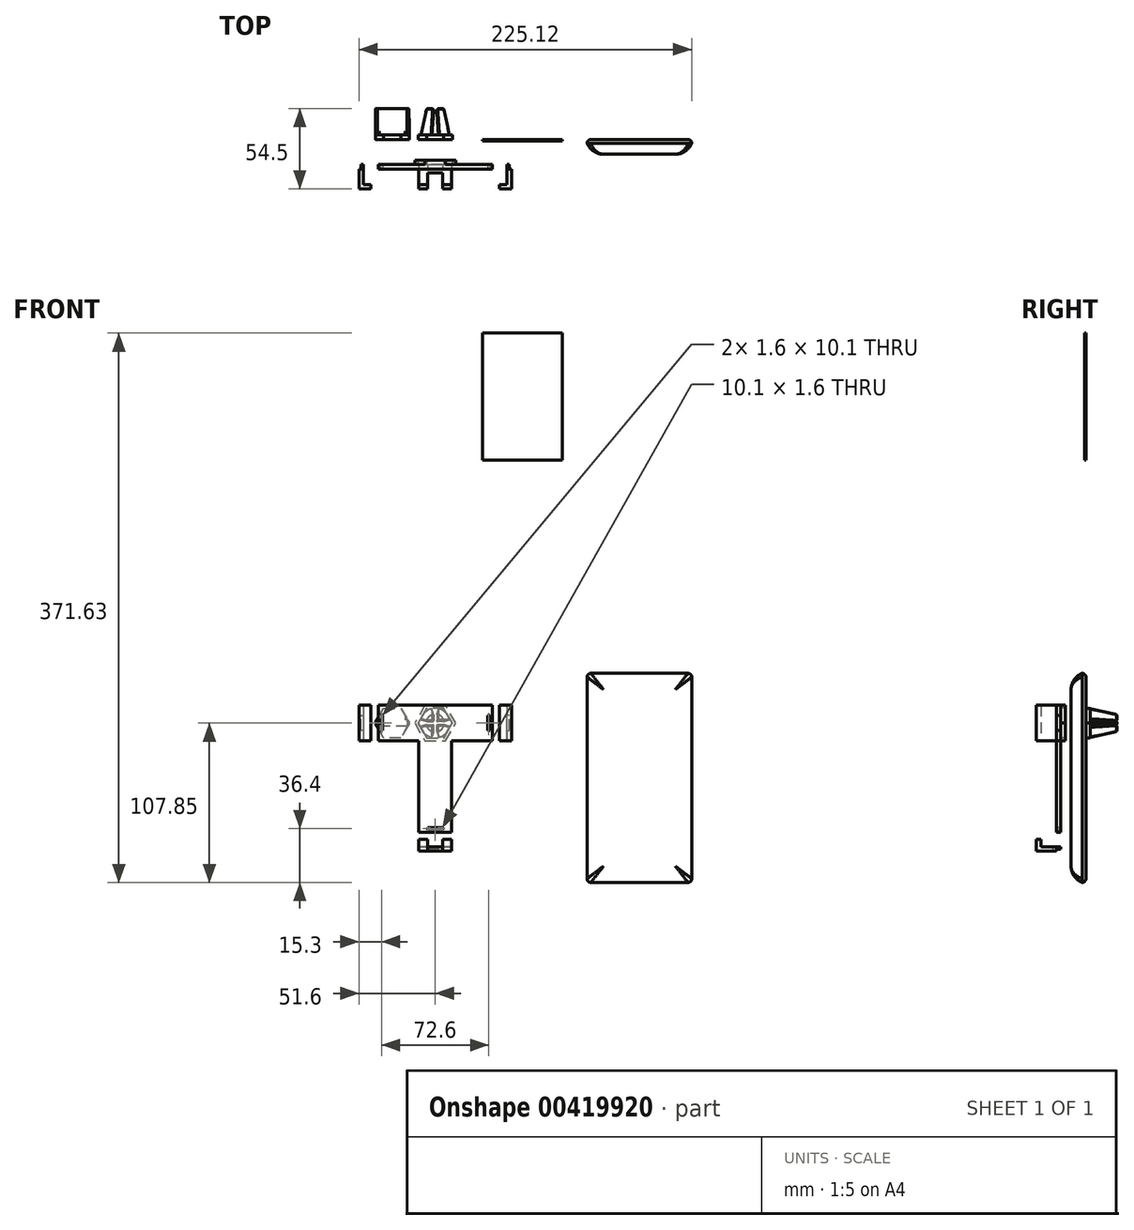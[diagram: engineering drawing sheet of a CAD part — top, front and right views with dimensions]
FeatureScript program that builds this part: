
annotation { "Feature Type Name" : "Feature", "Feature Type Description" : "" }
export const myFeature = defineFeature(function(context is Context, id is Id, definition is map)
    precondition{}
    {
        {
            assignVariable(context, id + "F0", {"name" : "depth_phone", "anyValue" : 10});
        }
        {
            var Q0;
            Q0=qCreatedBy(makeId("Front.planeOp"),FACE);
            var sketch = newSketch(context, id + "F1", { "sketchPlane" : qUnion([Q0])});
            skCircle(sketch, "E0", {"center": v(0, 0) * mm, "radius": 10 * mm});
            skSolve(sketch);
        }
        {
            var Q0;
            Q0=qSketchRegion(id+"F1",true);
            extrude(context, id + "F2", {"entities" : qUnion([Q0]), "oppositeDirection" : true, "depth" : 3 * mm});
        }
        {
            var Q0;
            Q0=makeQuery(id+"F2.opExtrude","CAP_FACE",FACE,{"disambiguationData":[OSD([sQuery(id+"F1.wireOp",EDGE,"E0")])],"isStart":false});
            var sketch = newSketch(context, id + "F3", { "sketchPlane" : qUnion([Q0])});
            skLineSegment(sketch, "E1.top", {"start": v(-9.75, 2.2) * mm, "end": v(-2.2, 2.2) * mm});
            skLineSegment(sketch, "E1.right", {"start": v(-2.2, 9.75) * mm, "end": v(-2.2, 2.2) * mm});
            skArc(sketch, "E2", {"start": v(-2.2, 9.75) * mm, "mid": v(-7.07, 7.07) * mm, "end": v(-9.75, 2.2) * mm});
            skLineSegment(sketch, "E3.1.0", {"start": v(-9.75, -2.2) * mm, "end": v(-2.2, -2.2) * mm});
            skLineSegment(sketch, "E3.1.1", {"start": v(-2.2, -9.75) * mm, "end": v(-2.2, -2.2) * mm});
            skArc(sketch, "E3.1.2", {"start": v(-9.75, -2.2) * mm, "mid": v(-7.07, -7.07) * mm, "end": v(-2.2, -9.75) * mm});
            skLineSegment(sketch, "E3.2.0", {"start": v(2.2, -9.75) * mm, "end": v(2.2, -2.2) * mm});
            skLineSegment(sketch, "E3.2.1", {"start": v(9.75, -2.2) * mm, "end": v(2.2, -2.2) * mm});
            skArc(sketch, "E3.2.2", {"start": v(2.2, -9.75) * mm, "mid": v(7.07, -7.07) * mm, "end": v(9.75, -2.2) * mm});
            skLineSegment(sketch, "E4.2.3.0", {"start": v(9.75, 2.2) * mm, "end": v(2.2, 2.2) * mm});
            skLineSegment(sketch, "E4.3.3.0", {"start": v(2.2, 9.75) * mm, "end": v(2.2, 2.2) * mm});
            skArc(sketch, "E4.6.3.0", {"start": v(9.75, 2.2) * mm, "mid": v(7.07, 7.07) * mm, "end": v(2.2, 9.75) * mm});
            skSolve(sketch);
        }
        {
            var Q0;
            Q0=makeQuery(id+"F3.imprint","IMPRINT",FACE,{"disambiguationData":[TD([[makeQuery(id+"F3.imprint","IMPRINT",EDGE,{"derivedFrom":sQuery(id+"F3.wireOp",EDGE,"E1.top")}),-1.0]])]});
            cPlane(context, id + "F4", {"entities" : qUnion([Q0]), "cplaneType" : CPlaneType.OFFSET, "offset" : 18 * mm, "width" : 150 * mm, "height" : 150 * mm});
        }
        {
            var Q0;
            Q0=qCreatedBy(id+"F4.planeOp",FACE);
            var sketch = newSketch(context, id + "F5", { "sketchPlane" : qUnion([Q0])});
            skLineSegment(sketch, "E5.top", {"start": v(-5.92, 1) * mm, "end": v(-1, 1) * mm});
            skLineSegment(sketch, "E5.right", {"start": v(-1, 5.92) * mm, "end": v(-1, 1) * mm});
            skArc(sketch, "E6", {"start": v(-1, 5.92) * mm, "mid": v(-4.24, 4.24) * mm, "end": v(-5.92, 1) * mm});
            skLineSegment(sketch, "E7.1.0", {"start": v(-5.92, -1) * mm, "end": v(-1, -1) * mm});
            skLineSegment(sketch, "E7.1.1", {"start": v(-1, -5.92) * mm, "end": v(-1, -1) * mm});
            skArc(sketch, "E7.1.2", {"start": v(-5.92, -1) * mm, "mid": v(-4.24, -4.24) * mm, "end": v(-1, -5.92) * mm});
            skLineSegment(sketch, "E7.2.0", {"start": v(1, -5.92) * mm, "end": v(1, -1) * mm});
            skLineSegment(sketch, "E7.2.1", {"start": v(5.92, -1) * mm, "end": v(1, -1) * mm});
            skArc(sketch, "E7.2.2", {"start": v(1, -5.92) * mm, "mid": v(4.24, -4.24) * mm, "end": v(5.92, -1) * mm});
            skLineSegment(sketch, "E7.3.0", {"start": v(5.92, 1) * mm, "end": v(1, 1) * mm});
            skLineSegment(sketch, "E7.3.1", {"start": v(1, 5.92) * mm, "end": v(1, 1) * mm});
            skArc(sketch, "E7.3.2", {"start": v(5.92, 1) * mm, "mid": v(4.24, 4.24) * mm, "end": v(1, 5.92) * mm});
            skSolve(sketch);
        }
        {
            var Q1;
            Q1=makeQuery(id+"F5.imprint","IMPRINT",FACE,{"disambiguationData":[TD([[makeQuery(id+"F5.imprint","IMPRINT",EDGE,{"derivedFrom":sQuery(id+"F5.wireOp",EDGE,"E5.top")}),1.0]])]});
            var Q2;
            Q2=makeQuery(id+"F3.imprint","IMPRINT",FACE,{"disambiguationData":[TD([[makeQuery(id+"F3.imprint","IMPRINT",EDGE,{"derivedFrom":sQuery(id+"F3.wireOp",EDGE,"E1.top")}),1.0]])]});
            loft(context, id + "F6", {"operationType" : NewBodyOperationType.ADD, "sheetProfilesArray" : [{ "sheetProfileEntities" : qUnion([Q1]) }, { "sheetProfileEntities" : qUnion([Q2]) }]});
        }
        {
            var Q1;
            Q1=makeQuery(id+"F3.imprint","IMPRINT",FACE,{"disambiguationData":[TD([[makeQuery(id+"F3.imprint","IMPRINT",EDGE,{"derivedFrom":sQuery(id+"F3.wireOp",EDGE,"E4.2.3.0")}),-1.0]])]});
            var Q2;
            Q2=makeQuery(id+"F5.imprint","IMPRINT",FACE,{"disambiguationData":[TD([[makeQuery(id+"F5.imprint","IMPRINT",EDGE,{"derivedFrom":sQuery(id+"F5.wireOp",EDGE,"E7.3.0")}),-1.0]])]});
            loft(context, id + "F7", {"operationType" : NewBodyOperationType.ADD, "sheetProfilesArray" : [{ "sheetProfileEntities" : qUnion([Q1]) }, { "sheetProfileEntities" : qUnion([Q2]) }]});
        }
        {
            var Q1;
            Q1=makeQuery(id+"F3.imprint","IMPRINT",FACE,{"disambiguationData":[TD([[makeQuery(id+"F3.imprint","IMPRINT",EDGE,{"derivedFrom":sQuery(id+"F3.wireOp",EDGE,"E3.1.0")}),-1.0]])]});
            var Q2;
            Q2=makeQuery(id+"F5.imprint","IMPRINT",FACE,{"disambiguationData":[TD([[makeQuery(id+"F5.imprint","IMPRINT",EDGE,{"derivedFrom":sQuery(id+"F5.wireOp",EDGE,"E7.1.0")}),-1.0]])]});
            loft(context, id + "F8", {"operationType" : NewBodyOperationType.ADD, "sheetProfilesArray" : [{ "sheetProfileEntities" : qUnion([Q1]) }, { "sheetProfileEntities" : qUnion([Q2]) }]});
        }
        {
            var Q1;
            Q1=makeQuery(id+"F3.imprint","IMPRINT",FACE,{"disambiguationData":[TD([[makeQuery(id+"F3.imprint","IMPRINT",EDGE,{"derivedFrom":sQuery(id+"F3.wireOp",EDGE,"E3.2.0")}),-1.0]])]});
            var Q2;
            Q2=makeQuery(id+"F5.imprint","IMPRINT",FACE,{"disambiguationData":[TD([[makeQuery(id+"F5.imprint","IMPRINT",EDGE,{"derivedFrom":sQuery(id+"F5.wireOp",EDGE,"E7.2.0")}),-1.0]])]});
            loft(context, id + "F9", {"operationType" : NewBodyOperationType.ADD, "sheetProfilesArray" : [{ "sheetProfileEntities" : qUnion([Q1]) }, { "sheetProfileEntities" : qUnion([Q2]) }]});
        }
        {
            var Q0;
            {var subQ0=sQuery(id+"F5.wireOp",EDGE,"E6");var subQ1=sQuery(id+"F5.wireOp",EDGE,"E5.right");var subQ2=sQuery(id+"F5.wireOp",EDGE,"E5.top");Q0=makeQuery(id+"F6.opLoft","MID_CAP_EDGE",EDGE,{"disambiguationData":[OSD([subQ2,subQ1,subQ0]),TDD([makeQuery(id+"F5.imprint","INTERSECT",VERTEX,{"derivedFrom":[subQ2,subQ0]}),makeQuery(id+"F5.imprint","INTERSECT",VERTEX,{"derivedFrom":[subQ1,subQ0]}),makeQuery(id+"F5.imprint","IMPRINT",EDGE,{"derivedFrom":subQ0})])],"capPos":0.0});}
            var Q1;
            Q1=makeQuery(id+"F6.opLoft","SWEPT_EDGE",EDGE,{"disambiguationData":[OSD([sQuery(id+"F3.wireOp",EDGE,"E1.right"),sQuery(id+"F3.wireOp",EDGE,"E2"),sQuery(id+"F5.wireOp",EDGE,"E5.right"),sQuery(id+"F5.wireOp",EDGE,"E6")])]});
            var Q2;
            Q2=makeQuery(id+"F6.opLoft","SWEPT_EDGE",EDGE,{"disambiguationData":[OSD([sQuery(id+"F3.wireOp",EDGE,"E1.top"),sQuery(id+"F3.wireOp",EDGE,"E1.right"),sQuery(id+"F5.wireOp",EDGE,"E5.top"),sQuery(id+"F5.wireOp",EDGE,"E5.right")])]});
            var Q3;
            Q3=makeQuery(id+"F6.opLoft","SWEPT_EDGE",EDGE,{"disambiguationData":[OSD([sQuery(id+"F3.wireOp",EDGE,"E1.top"),sQuery(id+"F3.wireOp",EDGE,"E2"),sQuery(id+"F5.wireOp",EDGE,"E5.top"),sQuery(id+"F5.wireOp",EDGE,"E6")])]});
            var Q4;
            {var subQ0=sQuery(id+"F5.wireOp",EDGE,"E7.1.2");var subQ1=sQuery(id+"F5.wireOp",EDGE,"E7.1.1");var subQ2=sQuery(id+"F5.wireOp",EDGE,"E7.1.0");Q4=makeQuery(id+"F8.opLoft","MID_CAP_EDGE",EDGE,{"disambiguationData":[OSD([subQ2,subQ1,subQ0]),TDD([makeQuery(id+"F5.imprint","INTERSECT",VERTEX,{"derivedFrom":[subQ2,subQ0]}),makeQuery(id+"F5.imprint","INTERSECT",VERTEX,{"derivedFrom":[subQ1,subQ0]}),makeQuery(id+"F5.imprint","IMPRINT",EDGE,{"derivedFrom":subQ0})])],"capPos":1.0});}
            var Q5;
            Q5=makeQuery(id+"F8.opLoft","SWEPT_EDGE",EDGE,{"disambiguationData":[OSD([sQuery(id+"F3.wireOp",EDGE,"E3.1.0"),sQuery(id+"F3.wireOp",EDGE,"E3.1.2"),sQuery(id+"F5.wireOp",EDGE,"E7.1.0"),sQuery(id+"F5.wireOp",EDGE,"E7.1.2")])]});
            var Q6;
            Q6=makeQuery(id+"F8.opLoft","SWEPT_EDGE",EDGE,{"disambiguationData":[OSD([sQuery(id+"F3.wireOp",EDGE,"E3.1.0"),sQuery(id+"F3.wireOp",EDGE,"E3.1.1"),sQuery(id+"F5.wireOp",EDGE,"E7.1.0"),sQuery(id+"F5.wireOp",EDGE,"E7.1.1")])]});
            var Q7;
            Q7=makeQuery(id+"F8.opLoft","SWEPT_EDGE",EDGE,{"disambiguationData":[OSD([sQuery(id+"F3.wireOp",EDGE,"E3.1.1"),sQuery(id+"F3.wireOp",EDGE,"E3.1.2"),sQuery(id+"F5.wireOp",EDGE,"E7.1.1"),sQuery(id+"F5.wireOp",EDGE,"E7.1.2")])]});
            var Q8;
            {var subQ0=sQuery(id+"F5.wireOp",EDGE,"E7.2.2");var subQ1=sQuery(id+"F5.wireOp",EDGE,"E7.2.1");var subQ2=sQuery(id+"F5.wireOp",EDGE,"E7.2.0");Q8=makeQuery(id+"F9.opLoft","MID_CAP_EDGE",EDGE,{"disambiguationData":[OSD([subQ2,subQ1,subQ0]),TDD([makeQuery(id+"F5.imprint","INTERSECT",VERTEX,{"derivedFrom":[subQ2,subQ0]}),makeQuery(id+"F5.imprint","INTERSECT",VERTEX,{"derivedFrom":[subQ1,subQ0]}),makeQuery(id+"F5.imprint","IMPRINT",EDGE,{"derivedFrom":subQ0})])],"capPos":1.0});}
            var Q9;
            Q9=makeQuery(id+"F9.opLoft","SWEPT_EDGE",EDGE,{"disambiguationData":[OSD([sQuery(id+"F3.wireOp",EDGE,"E3.2.0"),sQuery(id+"F3.wireOp",EDGE,"E3.2.2"),sQuery(id+"F5.wireOp",EDGE,"E7.2.0"),sQuery(id+"F5.wireOp",EDGE,"E7.2.2")])]});
            var Q10;
            Q10=makeQuery(id+"F9.opLoft","SWEPT_EDGE",EDGE,{"disambiguationData":[OSD([sQuery(id+"F3.wireOp",EDGE,"E3.2.1"),sQuery(id+"F3.wireOp",EDGE,"E3.2.2"),sQuery(id+"F5.wireOp",EDGE,"E7.2.1"),sQuery(id+"F5.wireOp",EDGE,"E7.2.2")])]});
            var Q11;
            Q11=makeQuery(id+"F9.opLoft","SWEPT_EDGE",EDGE,{"disambiguationData":[OSD([sQuery(id+"F3.wireOp",EDGE,"E3.2.0"),sQuery(id+"F3.wireOp",EDGE,"E3.2.1"),sQuery(id+"F5.wireOp",EDGE,"E7.2.0"),sQuery(id+"F5.wireOp",EDGE,"E7.2.1")])]});
            var Q12;
            {var subQ0=sQuery(id+"F5.wireOp",EDGE,"E7.3.2");var subQ1=sQuery(id+"F5.wireOp",EDGE,"E7.3.1");var subQ2=sQuery(id+"F5.wireOp",EDGE,"E7.3.0");Q12=makeQuery(id+"F7.opLoft","MID_CAP_EDGE",EDGE,{"disambiguationData":[OSD([subQ2,subQ1,subQ0]),TDD([makeQuery(id+"F5.imprint","INTERSECT",VERTEX,{"derivedFrom":[subQ2,subQ0]}),makeQuery(id+"F5.imprint","INTERSECT",VERTEX,{"derivedFrom":[subQ1,subQ0]}),makeQuery(id+"F5.imprint","IMPRINT",EDGE,{"derivedFrom":subQ0})])],"capPos":1.0});}
            var Q13;
            Q13=makeQuery(id+"F7.opLoft","SWEPT_EDGE",EDGE,{"disambiguationData":[OSD([sQuery(id+"F3.wireOp",EDGE,"E4.2.3.0"),sQuery(id+"F3.wireOp",EDGE,"E4.3.3.0"),sQuery(id+"F5.wireOp",EDGE,"E7.3.0"),sQuery(id+"F5.wireOp",EDGE,"E7.3.1")])]});
            var Q14;
            Q14=makeQuery(id+"F7.opLoft","SWEPT_EDGE",EDGE,{"disambiguationData":[OSD([sQuery(id+"F3.wireOp",EDGE,"E4.2.3.0"),sQuery(id+"F3.wireOp",EDGE,"E4.6.3.0"),sQuery(id+"F5.wireOp",EDGE,"E7.3.0"),sQuery(id+"F5.wireOp",EDGE,"E7.3.2")])]});
            var Q15;
            Q15=makeQuery(id+"F7.opLoft","SWEPT_EDGE",EDGE,{"disambiguationData":[OSD([sQuery(id+"F3.wireOp",EDGE,"E4.3.3.0"),sQuery(id+"F3.wireOp",EDGE,"E4.6.3.0"),sQuery(id+"F5.wireOp",EDGE,"E7.3.1"),sQuery(id+"F5.wireOp",EDGE,"E7.3.2")])]});
            fillet(context, id + "F10", {"entities" : qUnion([Q0, Q1, Q2, Q3, Q4, Q5, Q6, Q7, Q8, Q9, Q10, Q11, Q12, Q13, Q14, Q15]), "radius" : .5 * mm, "tangentPropagation" : true, "allowEdgeOverflow" : false});
        }
        {
            var Q0;
            Q0=qCreatedBy(makeId("Front.planeOp"),FACE);
            var sketch = newSketch(context, id + "F11", { "sketchPlane" : qUnion([Q0])});
            skLineSegment(sketch, "E8.bottom", {"start": v(86.03, 177.78) * mm, "end": v(32.03, 177.78) * mm});
            skLineSegment(sketch, "E8.top", {"start": v(86.03, 263.78) * mm, "end": v(32.03, 263.78) * mm});
            skLineSegment(sketch, "E8.left", {"start": v(86.03, 177.78) * mm, "end": v(86.03, 263.78) * mm});
            skLineSegment(sketch, "E8.right", {"start": v(32.03, 177.78) * mm, "end": v(32.03, 263.78) * mm});
            skSolve(sketch);
        }
        {
            var Q0;
            Q0=makeQuery(id+"F11.imprint","IMPRINT",FACE,{"disambiguationData":[TD([[makeQuery(id+"F11.imprint","IMPRINT",EDGE,{"derivedFrom":sQuery(id+"F11.wireOp",EDGE,"E8.bottom")}),-1.0]])]});
            extrude(context, id + "F12", {"entities" : qUnion([Q0]), "depth" : 1 * mm});
        }
        {
            var Q0;
            {var subQ0=sQuery(id+"F5.wireOp",EDGE,"E5.right");var subQ1=sQuery(id+"F5.wireOp",EDGE,"E6");var subQ2=sQuery(id+"F5.wireOp",EDGE,"E5.top");Q0=makeQuery(id+"F6.opLoft","MID_CAP_EDGE",EDGE,{"disambiguationData":[OSD([subQ2,subQ0,subQ1]),TDD([makeQuery(id+"F5.imprint","INTERSECT",VERTEX,{"derivedFrom":[subQ2,subQ0]}),makeQuery(id+"F5.imprint","INTERSECT",VERTEX,{"derivedFrom":[subQ0,subQ1]}),makeQuery(id+"F5.imprint","IMPRINT",EDGE,{"derivedFrom":subQ0})])],"capPos":0.0});}
            var Q1;
            {var subQ0=sQuery(id+"F5.wireOp",EDGE,"E5.top");var subQ1=sQuery(id+"F5.wireOp",EDGE,"E5.right");var subQ2=sQuery(id+"F5.wireOp",EDGE,"E6");Q1=makeQuery(id+"F6.opLoft","MID_CAP_EDGE",EDGE,{"disambiguationData":[OSD([subQ0,subQ1,subQ2]),TDD([makeQuery(id+"F5.imprint","INTERSECT",VERTEX,{"derivedFrom":[subQ0,subQ2]}),makeQuery(id+"F5.imprint","INTERSECT",VERTEX,{"derivedFrom":[subQ0,subQ1]}),makeQuery(id+"F5.imprint","IMPRINT",EDGE,{"derivedFrom":subQ0})])],"capPos":0.0});}
            var Q2;
            {var subQ0=sQuery(id+"F5.wireOp",EDGE,"E7.1.0");var subQ1=sQuery(id+"F5.wireOp",EDGE,"E7.1.1");var subQ2=sQuery(id+"F5.wireOp",EDGE,"E7.1.2");Q2=makeQuery(id+"F8.opLoft","MID_CAP_EDGE",EDGE,{"disambiguationData":[OSD([subQ0,subQ1,subQ2]),TDD([makeQuery(id+"F5.imprint","INTERSECT",VERTEX,{"derivedFrom":[subQ0,subQ2]}),makeQuery(id+"F5.imprint","INTERSECT",VERTEX,{"derivedFrom":[subQ0,subQ1]}),makeQuery(id+"F5.imprint","IMPRINT",EDGE,{"derivedFrom":subQ0})])],"capPos":1.0});}
            var Q3;
            {var subQ0=sQuery(id+"F5.wireOp",EDGE,"E7.1.1");var subQ1=sQuery(id+"F5.wireOp",EDGE,"E7.1.2");var subQ2=sQuery(id+"F5.wireOp",EDGE,"E7.1.0");Q3=makeQuery(id+"F8.opLoft","MID_CAP_EDGE",EDGE,{"disambiguationData":[OSD([subQ2,subQ0,subQ1]),TDD([makeQuery(id+"F5.imprint","INTERSECT",VERTEX,{"derivedFrom":[subQ2,subQ0]}),makeQuery(id+"F5.imprint","INTERSECT",VERTEX,{"derivedFrom":[subQ0,subQ1]}),makeQuery(id+"F5.imprint","IMPRINT",EDGE,{"derivedFrom":subQ0})])],"capPos":1.0});}
            var Q4;
            {var subQ0=sQuery(id+"F5.wireOp",EDGE,"E7.2.0");var subQ1=sQuery(id+"F5.wireOp",EDGE,"E7.2.1");var subQ2=sQuery(id+"F5.wireOp",EDGE,"E7.2.2");Q4=makeQuery(id+"F9.opLoft","MID_CAP_EDGE",EDGE,{"disambiguationData":[OSD([subQ0,subQ1,subQ2]),TDD([makeQuery(id+"F5.imprint","INTERSECT",VERTEX,{"derivedFrom":[subQ0,subQ2]}),makeQuery(id+"F5.imprint","INTERSECT",VERTEX,{"derivedFrom":[subQ0,subQ1]}),makeQuery(id+"F5.imprint","IMPRINT",EDGE,{"derivedFrom":subQ0})])],"capPos":1.0});}
            var Q5;
            {var subQ0=sQuery(id+"F5.wireOp",EDGE,"E7.2.1");var subQ1=sQuery(id+"F5.wireOp",EDGE,"E7.2.2");var subQ2=sQuery(id+"F5.wireOp",EDGE,"E7.2.0");Q5=makeQuery(id+"F9.opLoft","MID_CAP_EDGE",EDGE,{"disambiguationData":[OSD([subQ2,subQ0,subQ1]),TDD([makeQuery(id+"F5.imprint","INTERSECT",VERTEX,{"derivedFrom":[subQ2,subQ0]}),makeQuery(id+"F5.imprint","INTERSECT",VERTEX,{"derivedFrom":[subQ0,subQ1]}),makeQuery(id+"F5.imprint","IMPRINT",EDGE,{"derivedFrom":subQ0})])],"capPos":1.0});}
            var Q6;
            {var subQ0=sQuery(id+"F5.wireOp",EDGE,"E7.3.0");var subQ1=sQuery(id+"F5.wireOp",EDGE,"E7.3.1");var subQ2=sQuery(id+"F5.wireOp",EDGE,"E7.3.2");Q6=makeQuery(id+"F7.opLoft","MID_CAP_EDGE",EDGE,{"disambiguationData":[OSD([subQ0,subQ1,subQ2]),TDD([makeQuery(id+"F5.imprint","INTERSECT",VERTEX,{"derivedFrom":[subQ0,subQ2]}),makeQuery(id+"F5.imprint","INTERSECT",VERTEX,{"derivedFrom":[subQ0,subQ1]}),makeQuery(id+"F5.imprint","IMPRINT",EDGE,{"derivedFrom":subQ0})])],"capPos":1.0});}
            var Q7;
            {var subQ0=sQuery(id+"F5.wireOp",EDGE,"E7.3.1");var subQ1=sQuery(id+"F5.wireOp",EDGE,"E7.3.2");var subQ2=sQuery(id+"F5.wireOp",EDGE,"E7.3.0");Q7=makeQuery(id+"F7.opLoft","MID_CAP_EDGE",EDGE,{"disambiguationData":[OSD([subQ2,subQ0,subQ1]),TDD([makeQuery(id+"F5.imprint","INTERSECT",VERTEX,{"derivedFrom":[subQ2,subQ0]}),makeQuery(id+"F5.imprint","INTERSECT",VERTEX,{"derivedFrom":[subQ0,subQ1]}),makeQuery(id+"F5.imprint","IMPRINT",EDGE,{"derivedFrom":subQ0})])],"capPos":1.0});}
            fillet(context, id + "F13", {"entities" : qUnion([Q0, Q1, Q2, Q3, Q4, Q5, Q6, Q7]), "radius" : 1.5 * mm, "tangentPropagation" : true, "allowEdgeOverflow" : false});
        }
        {
            var Q0;
            Q0=qCreatedBy(makeId("Front.planeOp"),FACE);
            var sketch = newSketch(context, id + "F14", { "sketchPlane" : qUnion([Q0])});
            skLineSegment(sketch, "E9.bottom", {"start": v(102.82, 33.65) * mm, "end": v(173.52, 33.65) * mm});
            skLineSegment(sketch, "E9.top", {"start": v(102.82, -107.85) * mm, "end": v(173.52, -107.85) * mm});
            skLineSegment(sketch, "E9.left", {"start": v(102.82, 33.65) * mm, "end": v(102.82, -107.85) * mm});
            skLineSegment(sketch, "E9.right", {"start": v(173.52, 33.65) * mm, "end": v(173.52, -107.85) * mm});
            skSolve(sketch);
        }
        {
            var Q0;
            Q0=qSketchRegion(id+"F14",true);
            extrude(context, id + "F15", {"entities" : qUnion([Q0]), "depth" : (getVariable(context, 'depth_phone')) * mm});
        }
        {
            var Q0;
            Q0=makeQuery(id+"F15.opExtrude","SWEPT_EDGE",EDGE,{"disambiguationData":[OSD([sQuery(id+"F14.wireOp",EDGE,"E9.bottom"),sQuery(id+"F14.wireOp",EDGE,"E9.left")])]});
            var Q1;
            Q1=makeQuery(id+"F15.opExtrude","SWEPT_EDGE",EDGE,{"disambiguationData":[OSD([sQuery(id+"F14.wireOp",EDGE,"E9.bottom"),sQuery(id+"F14.wireOp",EDGE,"E9.right")])]});
            var Q2;
            Q2=makeQuery(id+"F15.opExtrude","SWEPT_EDGE",EDGE,{"disambiguationData":[OSD([sQuery(id+"F14.wireOp",EDGE,"E9.top"),sQuery(id+"F14.wireOp",EDGE,"E9.right")])]});
            var Q3;
            Q3=makeQuery(id+"F15.opExtrude","SWEPT_EDGE",EDGE,{"disambiguationData":[OSD([sQuery(id+"F14.wireOp",EDGE,"E9.top"),sQuery(id+"F14.wireOp",EDGE,"E9.left")])]});
            fillet(context, id + "F16", {"entities" : qUnion([Q0, Q1, Q2, Q3]), "radius" : 2.5 * mm, "tangentPropagation" : true, "allowEdgeOverflow" : false});
        }
        {
            var Q0;
            Q0=makeQuery(id+"F15.opExtrude","CAP_EDGE",EDGE,{"disambiguationData":[OSD([sQuery(id+"F14.wireOp",EDGE,"E9.right")])],"isStart":true});
            var Q1;
            Q1=makeQuery(id+"F15.opExtrude","CAP_EDGE",EDGE,{"disambiguationData":[OSD([sQuery(id+"F14.wireOp",EDGE,"E9.bottom")])],"isStart":true});
            var Q2;
            Q2=makeQuery(id+"F15.opExtrude","CAP_EDGE",EDGE,{"disambiguationData":[OSD([sQuery(id+"F14.wireOp",EDGE,"E9.left")])],"isStart":true});
            var Q3;
            Q3=makeQuery(id+"F15.opExtrude","CAP_EDGE",EDGE,{"disambiguationData":[OSD([sQuery(id+"F14.wireOp",EDGE,"E9.top")])],"isStart":true});
            fillet(context, id + "F17", {"entities" : qUnion([Q0, Q1, Q2, Q3]), "radius" : 2.5 * mm, "tangentPropagation" : true, "allowEdgeOverflow" : false});
        }
        {
            var Q0;
            Q0=makeQuery(id+"F15.opExtrude","CAP_EDGE",EDGE,{"disambiguationData":[OSD([sQuery(id+"F14.wireOp",EDGE,"E9.right")])],"isStart":false});
            var Q1;
            Q1=makeQuery(id+"F15.opExtrude","CAP_EDGE",EDGE,{"disambiguationData":[OSD([sQuery(id+"F14.wireOp",EDGE,"E9.bottom")])],"isStart":false});
            var Q2;
            Q2=makeQuery(id+"F15.opExtrude","CAP_EDGE",EDGE,{"disambiguationData":[OSD([sQuery(id+"F14.wireOp",EDGE,"E9.left")])],"isStart":false});
            var Q3;
            Q3=makeQuery(id+"F15.opExtrude","CAP_EDGE",EDGE,{"disambiguationData":[OSD([sQuery(id+"F14.wireOp",EDGE,"E9.top")])],"isStart":false});
            fillet(context, id + "F18", {"entities" : qUnion([Q0, Q1, Q2, Q3]), "radius" : 12 * mm, "tangentPropagation" : true, "allowEdgeOverflow" : false});
        }
        {
            var Q0;
            Q0=qCreatedBy(makeId("Front.planeOp"),FACE);
            cPlane(context, id + "F19", {"entities" : qUnion([Q0]), "cplaneType" : CPlaneType.OFFSET, "offset" : 20 * mm, "width" : 150 * mm, "height" : 150 * mm});
        }
        {
            var Q0;
            Q0=qCreatedBy(id+"F19.planeOp",FACE);
            var sketch = newSketch(context, id + "F20", { "sketchPlane" : qUnion([Q0])});
            skLineSegment(sketch, "E10.bottom", {"start": v(-11.1, -73.75) * mm, "end": v(11.1, -73.75) * mm});
            skLineSegment(sketch, "E10.top", {"start": v(-11.1, 0) * mm, "end": v(11.1, 0) * mm});
            skLineSegment(sketch, "E10.left", {"start": v(-11.1, -73.75) * mm, "end": v(-11.1, 0) * mm});
            skLineSegment(sketch, "E10.right", {"start": v(11.1, -73.75) * mm, "end": v(11.1, 0) * mm});
            skSolve(sketch);
        }
        {
            var Q0;
            Q0=qSketchRegion(id+"F20",true);
            extrude(context, id + "F21", {"entities" : qUnion([Q0]), "operationType" : NewBodyOperationType.ADD, "oppositeDirection" : true, "depth" : 3 * mm});
        }
        {
            var Q0;
            Q0=makeQuery(id+"F21.opExtrude","SWEPT_FACE",FACE,{"disambiguationData":[OSD([sQuery(id+"F20.wireOp",EDGE,"E10.bottom")])]});
            cPlane(context, id + "F22", {"entities" : qUnion([Q0]), "cplaneType" : CPlaneType.OFFSET, "offset" : 10 * mm, "width" : 150 * mm, "height" : 150 * mm});
        }
        {
            var Q0;
            Q0=qCreatedBy(id+"F22.planeOp",FACE);
            var sketch = newSketch(context, id + "F23", { "sketchPlane" : qUnion([Q0])});
            skLineSegment(sketch, "E11.bottom", {"start": v(11.1, 17) * mm, "end": v(-11.1, 17) * mm});
            skLineSegment(sketch, "E11.top", {"start": v(11.1, 30.5) * mm, "end": v(-11.1, 30.5) * mm});
            skLineSegment(sketch, "E11.left", {"start": v(11.1, 17) * mm, "end": v(11.1, 30.5) * mm});
            skLineSegment(sketch, "E11.right", {"start": v(-11.1, 17) * mm, "end": v(-11.1, 30.5) * mm});
            skSolve(sketch);
        }
        {
            var Q0;
            Q0=qSketchRegion(id+"F23",true);
            extrude(context, id + "F24", {"entities" : qUnion([Q0]), "operationType" : NewBodyOperationType.ADD, "depth" : 3 * mm});
        }
        {
            var Q0;
            Q0=qCreatedBy(id+"F19.planeOp",FACE);
            var sketch = newSketch(context, id + "F25", { "sketchPlane" : qUnion([Q0])});
            skLineSegment(sketch, "E12.bottom", {"start": v(38.6, 12) * mm, "end": v(-38.6, 12) * mm});
            skLineSegment(sketch, "E12.top", {"start": v(38.6, -12) * mm, "end": v(-38.6, -12) * mm});
            skLineSegment(sketch, "E12.left", {"start": v(38.6, 12) * mm, "end": v(38.6, -12) * mm});
            skLineSegment(sketch, "E12.right", {"start": v(-38.6, 12) * mm, "end": v(-38.6, -12) * mm});
            skLineSegment(sketch, "E13", {"start": v(38.6, 0) * mm, "end": v(-38.6, 0) * mm, "construction": true});
            skLineSegment(sketch, "E14", {"start": v(0, -12) * mm, "end": v(0, 12) * mm, "construction": true});
            skPoint(sketch, "E15", {"position": v(0, 0) * mm});
            skSolve(sketch);
        }
        {
            var Q0;
            Q0=makeQuery(id+"F25.imprint","IMPRINT",FACE,{"disambiguationData":[TD([[makeQuery(id+"F25.imprint","IMPRINT",EDGE,{"derivedFrom":sQuery(id+"F25.wireOp",EDGE,"E12.bottom")}),1.0]])]});
            extrude(context, id + "F26", {"entities" : qUnion([Q0]), "operationType" : NewBodyOperationType.ADD, "oppositeDirection" : true, "depth" : 3 * mm});
        }
        {
            var Q0;
            Q0=makeQuery(id+"F26.opExtrude","SWEPT_FACE",FACE,{"disambiguationData":[OSD([sQuery(id+"F25.wireOp",EDGE,"E12.right")])]});
            cPlane(context, id + "F27", {"entities" : qUnion([Q0]), "cplaneType" : CPlaneType.OFFSET, "offset" : 10 * mm, "width" : 150 * mm, "height" : 150 * mm});
        }
        {
            var Q0;
            Q0=qCreatedBy(id+"F27.planeOp",FACE);
            var sketch = newSketch(context, id + "F28", { "sketchPlane" : qUnion([Q0])});
            skLineSegment(sketch, "E16.bottom", {"start": v(17, 12) * mm, "end": v(30.5, 12) * mm});
            skLineSegment(sketch, "E16.top", {"start": v(17, -12) * mm, "end": v(30.5, -12) * mm});
            skLineSegment(sketch, "E16.left", {"start": v(17, 12) * mm, "end": v(17, -12) * mm});
            skLineSegment(sketch, "E16.right", {"start": v(30.5, 12) * mm, "end": v(30.5, -12) * mm});
            skSolve(sketch);
        }
        {
            var Q0;
            Q0=qSketchRegion(id+"F28",true);
            extrude(context, id + "F29", {"entities" : qUnion([Q0]), "operationType" : NewBodyOperationType.ADD, "depth" : 3 * mm});
        }
        {
            var Q0;
            Q0=makeQuery(id+"F26.opExtrude","SWEPT_FACE",FACE,{"disambiguationData":[OSD([sQuery(id+"F25.wireOp",EDGE,"E12.left")])]});
            cPlane(context, id + "F30", {"entities" : qUnion([Q0]), "cplaneType" : CPlaneType.OFFSET, "offset" : 10 * mm, "width" : 150 * mm, "height" : 150 * mm});
        }
        {
            var Q0;
            Q0=qCreatedBy(id+"F30.planeOp",FACE);
            var sketch = newSketch(context, id + "F31", { "sketchPlane" : qUnion([Q0])});
            skLineSegment(sketch, "E17.bottom", {"start": v(-17, -12) * mm, "end": v(-30.5, -12) * mm});
            skLineSegment(sketch, "E17.top", {"start": v(-17, 12) * mm, "end": v(-30.5, 12) * mm});
            skLineSegment(sketch, "E17.left", {"start": v(-17, -12) * mm, "end": v(-17, 12) * mm});
            skLineSegment(sketch, "E17.right", {"start": v(-30.5, -12) * mm, "end": v(-30.5, 12) * mm});
            skSolve(sketch);
        }
        {
            var Q0;
            Q0=qSketchRegion(id+"F31",true);
            extrude(context, id + "F32", {"entities" : qUnion([Q0]), "operationType" : NewBodyOperationType.ADD, "depth" : 3 * mm});
        }
        {
            var Q0;
            Q0=makeQuery(id+"F24.opExtrude","CAP_FACE",FACE,{"disambiguationData":[OSD([sQuery(id+"F23.wireOp",EDGE,"E11.bottom"),sQuery(id+"F23.wireOp",EDGE,"E11.top"),sQuery(id+"F23.wireOp",EDGE,"E11.left"),sQuery(id+"F23.wireOp",EDGE,"E11.right")])],"isStart":false});
            var sketch = newSketch(context, id + "F33", { "sketchPlane" : qUnion([Q0])});
            skLineSegment(sketch, "E18.bottom", {"start": v(-5.1, 30.5) * mm, "end": v(5.1, 30.5) * mm});
            skLineSegment(sketch, "E18.top", {"start": v(-5.1, 20) * mm, "end": v(5.1, 20) * mm});
            skLineSegment(sketch, "E18.left", {"start": v(-5.1, 30.5) * mm, "end": v(-5.1, 20) * mm});
            skLineSegment(sketch, "E18.right", {"start": v(5.1, 30.5) * mm, "end": v(5.1, 20) * mm});
            skLineSegment(sketch, "E19", {"start": v(0, 20) * mm, "end": v(0, 30.5) * mm, "construction": true});
            skSolve(sketch);
        }
        {
            var Q0;
            Q0=qSketchRegion(id+"F33",true);
            extrude(context, id + "F34", {"entities" : qUnion([Q0]), "operationType" : NewBodyOperationType.REMOVE, "endBound" : BoundingType.UP_TO_NEXT, "oppositeDirection" : true, "depth" : 25 * mm});
        }
        {
            var Q0;
            Q0=makeQuery(id+"F29.opExtrude","SWEPT_FACE",FACE,{"disambiguationData":[OSD([sQuery(id+"F28.wireOp",EDGE,"E16.right")])]});
            var sketch = newSketch(context, id + "F35", { "sketchPlane" : qUnion([Q0])});
            skLineSegment(sketch, "E20.bottom", {"start": v(-51.6, -12) * mm, "end": v(-43.6, -12) * mm});
            skLineSegment(sketch, "E20.top", {"start": v(-51.6, 12) * mm, "end": v(-43.6, 12) * mm});
            skLineSegment(sketch, "E20.left", {"start": v(-51.6, -12) * mm, "end": v(-51.6, 12) * mm});
            skLineSegment(sketch, "E20.right", {"start": v(-43.6, -12) * mm, "end": v(-43.6, 12) * mm});
            skLineSegment(sketch, "E21.bottom", {"start": v(51.6, -12) * mm, "end": v(43.6, -12) * mm});
            skLineSegment(sketch, "E21.top", {"start": v(51.6, 12) * mm, "end": v(43.6, 12) * mm});
            skLineSegment(sketch, "E21.left", {"start": v(51.6, -12) * mm, "end": v(51.6, 12) * mm});
            skLineSegment(sketch, "E21.right", {"start": v(43.6, -12) * mm, "end": v(43.6, 12) * mm});
            skLineSegment(sketch, "E22.bottom", {"start": v(-11.1, -86.75) * mm, "end": v(-5.1, -86.75) * mm});
            skLineSegment(sketch, "E22.top", {"start": v(-11.1, -78.75) * mm, "end": v(-5.1, -78.75) * mm});
            skLineSegment(sketch, "E22.left", {"start": v(-11.1, -86.75) * mm, "end": v(-11.1, -78.75) * mm});
            skLineSegment(sketch, "E22.right", {"start": v(-5.1, -86.75) * mm, "end": v(-5.1, -78.75) * mm});
            skLineSegment(sketch, "E23.bottom", {"start": v(5.1, -86.75) * mm, "end": v(11.1, -86.75) * mm});
            skLineSegment(sketch, "E23.top", {"start": v(5.1, -78.75) * mm, "end": v(11.1, -78.75) * mm});
            skLineSegment(sketch, "E23.left", {"start": v(5.1, -86.75) * mm, "end": v(5.1, -78.75) * mm});
            skLineSegment(sketch, "E23.right", {"start": v(11.1, -86.75) * mm, "end": v(11.1, -78.75) * mm});
            skSolve(sketch);
        }
        {
            var Q0;
            Q0=qSketchRegion(id+"F35",true);
            extrude(context, id + "F36", {"entities" : qUnion([Q0]), "operationType" : NewBodyOperationType.ADD, "depth" : 3 * mm});
        }
        {
            var Q0;
            Q0=makeQuery(id+"F32.boolean.opBoolean","MERGE",FACE,{"derivedFrom":[makeQuery(id+"F29.boolean.opBoolean","MERGE",FACE,{"derivedFrom":[makeQuery(id+"F26.boolean.opBoolean","MERGE",FACE,{"derivedFrom":[makeQuery(id+"F24.boolean.opBoolean","MERGE",FACE,{"derivedFrom":[makeQuery(id+"F21.opExtrude","CAP_FACE",FACE,{"disambiguationData":[OSD([sQuery(id+"F20.wireOp",EDGE,"E10.bottom"),sQuery(id+"F20.wireOp",EDGE,"E10.top"),sQuery(id+"F20.wireOp",EDGE,"E10.left"),sQuery(id+"F20.wireOp",EDGE,"E10.right")])],"isStart":false}),makeQuery(id+"F24.opExtrude","SWEPT_FACE",FACE,{"disambiguationData":[OSD([sQuery(id+"F23.wireOp",EDGE,"E11.bottom")])]})]}),makeQuery(id+"F26.opExtrude","CAP_FACE",FACE,{"disambiguationData":[OSD([sQuery(id+"F25.wireOp",EDGE,"E12.bottom"),sQuery(id+"F25.wireOp",EDGE,"E12.top"),sQuery(id+"F25.wireOp",EDGE,"E12.left"),sQuery(id+"F25.wireOp",EDGE,"E12.right")])],"isStart":false})]}),makeQuery(id+"F29.opExtrude","SWEPT_FACE",FACE,{"disambiguationData":[OSD([sQuery(id+"F28.wireOp",EDGE,"E16.left")])]})]}),makeQuery(id+"F32.opExtrude","SWEPT_FACE",FACE,{"disambiguationData":[OSD([sQuery(id+"F31.wireOp",EDGE,"E17.left")])]})]});
            var sketch = newSketch(context, id + "F37", { "sketchPlane" : qUnion([Q0])});
            skCircle(sketch, "E24.cCircle", {"center": v(0, 0) * mm, "radius": 10.1 * mm, "construction": true});
            skLineSegment(sketch, "E24.0", {"start": v(11.66, 0) * mm, "end": v(5.83, -10.1) * mm});
            skLineSegment(sketch, "E24.1", {"start": v(5.83, -10.1) * mm, "end": v(-5.83, -10.1) * mm});
            skLineSegment(sketch, "E24.2", {"start": v(-5.83, -10.1) * mm, "end": v(-11.66, 0) * mm});
            skLineSegment(sketch, "E24.3", {"start": v(-11.66, 0) * mm, "end": v(-5.83, 10.1) * mm});
            skLineSegment(sketch, "E24.4", {"start": v(-5.83, 10.1) * mm, "end": v(5.83, 10.1) * mm});
            skLineSegment(sketch, "E24.5", {"start": v(5.83, 10.1) * mm, "end": v(11.66, 0) * mm});
            skPoint(sketch, "E24.0.midPoint", {"position": v(8.75, -5.05) * mm});
            skCircle(sketch, "E25.cCircle", {"center": v(0, 0) * mm, "radius": 12 * mm, "construction": true});
            skLineSegment(sketch, "E25.0", {"start": v(13.86, 0) * mm, "end": v(6.93, -12) * mm});
            skLineSegment(sketch, "E25.1", {"start": v(6.93, -12) * mm, "end": v(-6.93, -12) * mm});
            skLineSegment(sketch, "E25.2", {"start": v(-6.93, -12) * mm, "end": v(-13.86, 0) * mm});
            skLineSegment(sketch, "E25.3", {"start": v(-13.86, 0) * mm, "end": v(-6.93, 12) * mm});
            skLineSegment(sketch, "E25.4", {"start": v(-6.93, 12) * mm, "end": v(6.93, 12) * mm});
            skLineSegment(sketch, "E25.5", {"start": v(6.93, 12) * mm, "end": v(13.86, 0) * mm});
            skPoint(sketch, "E25.0.midPoint", {"position": v(10.4, -6) * mm});
            skSolve(sketch);
        }
        {
            var Q0;
            Q0=qSketchRegion(id+"F37",true);
            extrude(context, id + "F38", {"entities" : qUnion([Q0]), "operationType" : NewBodyOperationType.ADD, "depth" : 3 * mm});
        }
        {
            var Q0;
            Q0=makeQuery(id+"F2.opExtrude","CAP_FACE",FACE,{"disambiguationData":[OSD([sQuery(id+"F1.wireOp",EDGE,"E0")])],"isStart":false});
            var sketch = newSketch(context, id + "F39", { "sketchPlane" : qUnion([Q0])});
            skCircle(sketch, "E26.cCircle", {"center": v(0, 0) * mm, "radius": 10 * mm, "construction": true});
            skLineSegment(sketch, "E26.0", {"start": v(11.55, 0) * mm, "end": v(5.77, -10) * mm});
            skLineSegment(sketch, "E26.1", {"start": v(5.77, -10) * mm, "end": v(-5.77, -10) * mm});
            skLineSegment(sketch, "E26.2", {"start": v(-5.77, -10) * mm, "end": v(-11.55, 0) * mm});
            skLineSegment(sketch, "E26.3", {"start": v(-11.55, 0) * mm, "end": v(-5.77, 10) * mm});
            skLineSegment(sketch, "E26.4", {"start": v(-5.77, 10) * mm, "end": v(5.77, 10) * mm});
            skLineSegment(sketch, "E26.5", {"start": v(5.77, 10) * mm, "end": v(11.55, 0) * mm});
            skPoint(sketch, "E26.0.midPoint", {"position": v(8.66, -5) * mm});
            skSolve(sketch);
        }
        {
            var Q0;
            Q0=qSketchRegion(id+"F39",true);
            extrude(context, id + "F40", {"entities" : qUnion([Q0]), "operationType" : NewBodyOperationType.ADD, "oppositeDirection" : true, "depth" : 3 * mm});
        }
        {
            var Q0;
            Q0=makeQuery(id+"F26.boolean.opBoolean","MERGE",FACE,{"derivedFrom":[makeQuery(id+"F21.opExtrude","CAP_FACE",FACE,{"disambiguationData":[OSD([sQuery(id+"F20.wireOp",EDGE,"E10.bottom"),sQuery(id+"F20.wireOp",EDGE,"E10.top"),sQuery(id+"F20.wireOp",EDGE,"E10.left"),sQuery(id+"F20.wireOp",EDGE,"E10.right")])],"isStart":true}),makeQuery(id+"F26.opExtrude","CAP_FACE",FACE,{"disambiguationData":[OSD([sQuery(id+"F25.wireOp",EDGE,"E12.bottom"),sQuery(id+"F25.wireOp",EDGE,"E12.top"),sQuery(id+"F25.wireOp",EDGE,"E12.left"),sQuery(id+"F25.wireOp",EDGE,"E12.right")])],"isStart":true})]});
            var sketch = newSketch(context, id + "F41", { "sketchPlane" : qUnion([Q0])});
            skLineSegment(sketch, "E27.bottom", {"start": v(-37.1, 5.05) * mm, "end": v(-35.5, 5.05) * mm});
            skLineSegment(sketch, "E27.top", {"start": v(-37.1, -5.05) * mm, "end": v(-35.5, -5.05) * mm});
            skLineSegment(sketch, "E27.left", {"start": v(-37.1, 5.05) * mm, "end": v(-37.1, -5.05) * mm});
            skLineSegment(sketch, "E27.right", {"start": v(-35.5, 5.05) * mm, "end": v(-35.5, -5.05) * mm});
            skLineSegment(sketch, "E28", {"start": v(-37.1, 0) * mm, "end": v(-35.5, 0) * mm, "construction": true});
            skLineSegment(sketch, "E29", {"start": v(0, 8.73) * mm, "end": v(0, 0) * mm, "construction": true});
            skLineSegment(sketch, "E30.MirrorCS", {"start": v(35.5, 5.05) * mm, "end": v(35.5, -5.05) * mm});
            skLineSegment(sketch, "E31.MirrorCS", {"start": v(37.1, -5.05) * mm, "end": v(35.5, -5.05) * mm});
            skLineSegment(sketch, "E32.MirrorCS", {"start": v(37.1, 5.05) * mm, "end": v(37.1, -5.05) * mm});
            skLineSegment(sketch, "E33.MirrorCS", {"start": v(37.1, 5.05) * mm, "end": v(35.5, 5.05) * mm});
            skLineSegment(sketch, "E34.bottom", {"start": v(-5.05, -72.25) * mm, "end": v(5.05, -72.25) * mm});
            skLineSegment(sketch, "E34.top", {"start": v(-5.05, -70.65) * mm, "end": v(5.05, -70.65) * mm});
            skLineSegment(sketch, "E34.left", {"start": v(-5.05, -72.25) * mm, "end": v(-5.05, -70.65) * mm});
            skLineSegment(sketch, "E34.right", {"start": v(5.05, -72.25) * mm, "end": v(5.05, -70.65) * mm});
            skLineSegment(sketch, "E35", {"start": v(0, -70.65) * mm, "end": v(0, -72.25) * mm, "construction": true});
            skSolve(sketch);
        }
        {
            var Q0;
            Q0=qSketchRegion(id+"F41",true);
            extrude(context, id + "F42", {"entities" : qUnion([Q0]), "operationType" : NewBodyOperationType.REMOVE, "endBound" : BoundingType.UP_TO_NEXT, "oppositeDirection" : true, "depth" : 25 * mm});
        }
        {
            var Q0;
            Q0=qCreatedBy(id+"F19.planeOp",FACE);
            var sketch = newSketch(context, id + "F43", { "sketchPlane" : qUnion([Q0])});
            skLineSegment(sketch, "E36", {"start": v(51.6, -12) * mm, "end": v(51.6, 12) * mm});
            skLineSegment(sketch, "E37", {"start": v(51.6, 12) * mm, "end": v(48.6, 12) * mm});
            skLineSegment(sketch, "E38", {"start": v(48.6, 12) * mm, "end": v(48.6, 5) * mm});
            skLineSegment(sketch, "E39", {"start": v(48.6, 5) * mm, "end": v(50.1, 5) * mm});
            skLineSegment(sketch, "E40", {"start": v(50.1, 5) * mm, "end": v(50.1, -5) * mm});
            skLineSegment(sketch, "E41", {"start": v(50.1, -5) * mm, "end": v(48.6, -5) * mm});
            skLineSegment(sketch, "E42", {"start": v(48.6, -5) * mm, "end": v(48.6, -12) * mm});
            skLineSegment(sketch, "E43", {"start": v(48.6, -12) * mm, "end": v(51.6, -12) * mm});
            skLineSegment(sketch, "E44", {"start": v(50.1, 0) * mm, "end": v(40.9, 0) * mm, "construction": true});
            skLineSegment(sketch, "E45", {"start": v(0, 0) * mm, "end": v(0, -18) * mm, "construction": true});
            skLineSegment(sketch, "E46.MirrorCS", {"start": v(-51.6, -12) * mm, "end": v(-51.6, 12) * mm});
            skLineSegment(sketch, "E47.MirrorCS", {"start": v(-51.6, 12) * mm, "end": v(-48.6, 12) * mm});
            skLineSegment(sketch, "E48.MirrorCS", {"start": v(-48.6, 12) * mm, "end": v(-48.6, 5) * mm});
            skLineSegment(sketch, "E49.MirrorCS", {"start": v(-48.6, 5) * mm, "end": v(-50.1, 5) * mm});
            skLineSegment(sketch, "E50.MirrorCS", {"start": v(-50.1, 5) * mm, "end": v(-50.1, -5) * mm});
            skLineSegment(sketch, "E51.MirrorCS", {"start": v(-50.1, -5) * mm, "end": v(-48.6, -5) * mm});
            skLineSegment(sketch, "E52.MirrorCS", {"start": v(-48.6, -5) * mm, "end": v(-48.6, -12) * mm});
            skLineSegment(sketch, "E53.MirrorCS", {"start": v(-48.6, -12) * mm, "end": v(-51.6, -12) * mm});
            skLineSegment(sketch, "E54", {"start": v(11.1, -86.75) * mm, "end": v(-11.1, -86.75) * mm});
            skLineSegment(sketch, "E55", {"start": v(-11.1, -86.75) * mm, "end": v(-11.1, -83.75) * mm});
            skLineSegment(sketch, "E56", {"start": v(-11.1, -83.75) * mm, "end": v(-5, -83.75) * mm});
            skLineSegment(sketch, "E57", {"start": v(-5, -83.75) * mm, "end": v(-5, -85.25) * mm});
            skLineSegment(sketch, "E58", {"start": v(-5, -85.25) * mm, "end": v(5, -85.25) * mm});
            skLineSegment(sketch, "E59", {"start": v(5, -85.25) * mm, "end": v(5, -83.75) * mm});
            skLineSegment(sketch, "E60", {"start": v(5, -83.75) * mm, "end": v(11.1, -83.75) * mm});
            skLineSegment(sketch, "E61", {"start": v(11.1, -83.75) * mm, "end": v(11.1, -86.75) * mm});
            skLineSegment(sketch, "E62", {"start": v(0, -85.25) * mm, "end": v(0, -78.2) * mm, "construction": true});
            skSolve(sketch);
        }
        {
            var Q0;
            Q0=qSketchRegion(id+"F43",true);
            extrude(context, id + "F44", {"entities" : qUnion([Q0]), "operationType" : NewBodyOperationType.REMOVE, "endBound" : BoundingType.UP_TO_NEXT, "oppositeDirection" : true, "depth" : 25 * mm});
        }
        {
            var Q0;
            {var subQ2=sQuery(id+"F35.wireOp",EDGE,"E22.bottom");var subQ3=sQuery(id+"F23.wireOp",EDGE,"E11.right");Q0=makeQuery(id+"F44.boolean.opBoolean","SPLIT",FACE,{"disambiguationData":[TD([makeQuery(id+"F24.opExtrude","SWEPT_FACE",FACE,{"disambiguationData":[OSD([subQ3])]})])],"derivedFrom":makeQuery(id+"F36.boolean.opBoolean","MERGE",FACE,{"derivedFrom":[makeQuery(id+"F24.opExtrude","CAP_FACE",FACE,{"disambiguationData":[OSD([sQuery(id+"F23.wireOp",EDGE,"E11.bottom"),sQuery(id+"F23.wireOp",EDGE,"E11.top"),sQuery(id+"F23.wireOp",EDGE,"E11.left"),subQ3])],"isStart":false}),makeQuery(id+"F36.opExtrude","SWEPT_FACE",FACE,{"disambiguationData":[OSD([subQ2])]}),makeQuery(id+"F36.opExtrude","SWEPT_FACE",FACE,{"disambiguationData":[OSD([sQuery(id+"F35.wireOp",EDGE,"E23.bottom")])]})]})});}
            var sketch = newSketch(context, id + "F45", { "sketchPlane" : qUnion([Q0])});
            skLineSegment(sketch, "E63.bottom", {"start": v(-5.1, 22.5) * mm, "end": v(5.1, 22.5) * mm});
            skLineSegment(sketch, "E63.top", {"start": v(-5.1, 20) * mm, "end": v(5.1, 20) * mm});
            skLineSegment(sketch, "E63.left", {"start": v(-5.1, 22.5) * mm, "end": v(-5.1, 20) * mm});
            skLineSegment(sketch, "E63.right", {"start": v(5.1, 22.5) * mm, "end": v(5.1, 20) * mm});
            skSolve(sketch);
        }
        {
            var Q0;
            Q0=qSketchRegion(id+"F45",true);
            extrude(context, id + "F46", {"entities" : qUnion([Q0]), "operationType" : NewBodyOperationType.ADD, "oppositeDirection" : true, "depth" : 3 * mm});
        }
        {
            var Q0;
            Q0=qCreatedBy(makeId("Front.planeOp"),FACE);
            var sketch = newSketch(context, id + "F47", { "sketchPlane" : qUnion([Q0])});
            skCircle(sketch, "E64.cCircle", {"center": v(-29.05, 0) * mm, "radius": 10 * mm, "construction": true});
            skLineSegment(sketch, "E64.0", {"start": v(-34.82, -10) * mm, "end": v(-40.6, 0) * mm});
            skLineSegment(sketch, "E64.1", {"start": v(-40.6, 0) * mm, "end": v(-34.82, 10) * mm});
            skLineSegment(sketch, "E64.2", {"start": v(-34.82, 10) * mm, "end": v(-23.28, 10) * mm});
            skLineSegment(sketch, "E64.3", {"start": v(-23.28, 10) * mm, "end": v(-17.5, 0) * mm});
            skLineSegment(sketch, "E64.4", {"start": v(-17.5, 0) * mm, "end": v(-23.28, -10) * mm});
            skLineSegment(sketch, "E64.5", {"start": v(-23.28, -10) * mm, "end": v(-34.82, -10) * mm});
            skPoint(sketch, "E64.0.midPoint", {"position": v(-37.71, -5) * mm});
            skSolve(sketch);
        }
        {
            var Q0;
            Q0=qSketchRegion(id+"F47",true);
            extrude(context, id + "F48", {"entities" : qUnion([Q0]), "oppositeDirection" : true, "depth" : 3 * mm});
        }
        {
            var Q0;
            Q0=makeQuery(id+"F48.opExtrude","CAP_FACE",FACE,{"disambiguationData":[OSD([sQuery(id+"F47.wireOp",EDGE,"E64.0"),sQuery(id+"F47.wireOp",EDGE,"E64.1"),sQuery(id+"F47.wireOp",EDGE,"E64.2"),sQuery(id+"F47.wireOp",EDGE,"E64.3"),sQuery(id+"F47.wireOp",EDGE,"E64.4"),sQuery(id+"F47.wireOp",EDGE,"E64.5")])],"isStart":false});
            var sketch = newSketch(context, id + "F49", { "sketchPlane" : qUnion([Q0])});
            skLineSegment(sketch, "E65", {"start": v(17.5, 0) * mm, "end": v(40.6, 0) * mm, "construction": true});
            skLineSegment(sketch, "E66", {"start": v(18.77, 2.2) * mm, "end": v(39.33, 2.2) * mm});
            skLineSegment(sketch, "E67.MirrorCS", {"start": v(18.77, -2.2) * mm, "end": v(39.33, -2.2) * mm});
            skLineSegment(sketch, "E68", {"start": v(18.77, 2.2) * mm, "end": v(17.5, 0) * mm});
            skLineSegment(sketch, "E69", {"start": v(17.5, 0) * mm, "end": v(18.77, -2.2) * mm});
            skLineSegment(sketch, "E70", {"start": v(39.33, -2.2) * mm, "end": v(40.6, 0) * mm});
            skLineSegment(sketch, "E71", {"start": v(40.6, 0) * mm, "end": v(39.33, 2.2) * mm});
            skSolve(sketch);
        }
        {
            var Q0;
            Q0=qCreatedBy(id+"F4.planeOp",FACE);
            var sketch = newSketch(context, id + "F50", { "sketchPlane" : qUnion([Q0])});
            skLineSegment(sketch, "E72", {"start": v(17.5, 0) * mm, "end": v(40.6, 0) * mm, "construction": true});
            skLineSegment(sketch, "E73", {"start": v(18.77, 1) * mm, "end": v(39.33, 1) * mm});
            skLineSegment(sketch, "E74", {"start": v(18.77, 3.44) * mm, "end": v(18.77, 1) * mm, "construction": true});
            skLineSegment(sketch, "E75", {"start": v(39.33, 2.62) * mm, "end": v(39.33, 1) * mm, "construction": true});
            skLineSegment(sketch, "E76.MirrorCS", {"start": v(18.77, -1) * mm, "end": v(39.33, -1) * mm});
            skLineSegment(sketch, "E77.trimOffspring", {"start": v(18.77, -1) * mm, "end": v(18.77, -3.73) * mm, "construction": true});
            skLineSegment(sketch, "E78.trimOffspring", {"start": v(39.33, -1) * mm, "end": v(39.33, -2.87) * mm, "construction": true});
            skLineSegment(sketch, "E79", {"start": v(18.77, 1) * mm, "end": v(17.5, 0) * mm});
            skLineSegment(sketch, "E80", {"start": v(18.77, -1) * mm, "end": v(17.5, 0) * mm});
            skLineSegment(sketch, "E81", {"start": v(39.33, -1) * mm, "end": v(40.6, 0) * mm});
            skLineSegment(sketch, "E82", {"start": v(40.6, 0) * mm, "end": v(39.33, 1) * mm});
            skSolve(sketch);
        }
        {
            var Q1;
            Q1=makeQuery(id+"F49.imprint","IMPRINT",FACE,{"disambiguationData":[TD([[makeQuery(id+"F49.imprint","IMPRINT",EDGE,{"derivedFrom":sQuery(id+"F49.wireOp",EDGE,"E66")}),-1.0]])]});
            var Q2;
            Q2=makeQuery(id+"F50.imprint","IMPRINT",FACE,{"disambiguationData":[TD([[makeQuery(id+"F50.imprint","IMPRINT",EDGE,{"derivedFrom":sQuery(id+"F50.wireOp",EDGE,"E73")}),-1.0]])]});
            loft(context, id + "F51", {"operationType" : NewBodyOperationType.ADD, "sheetProfilesArray" : [{ "sheetProfileEntities" : qUnion([Q1]) }, { "sheetProfileEntities" : qUnion([Q2]) }]});
        }
        {
            var Q0;
            Q0=makeQuery(id+"F51.opLoft","SWEPT_EDGE",EDGE,{"disambiguationData":[OSD([sQuery(id+"F49.wireOp",EDGE,"E68"),sQuery(id+"F49.wireOp",EDGE,"E69"),sQuery(id+"F50.wireOp",EDGE,"E79"),sQuery(id+"F50.wireOp",EDGE,"E80")])]});
            var Q1;
            Q1=makeQuery(id+"F51.opLoft","SWEPT_EDGE",EDGE,{"disambiguationData":[OSD([sQuery(id+"F47.wireOp",EDGE,"E64.4"),sQuery(id+"F49.wireOp",EDGE,"E67.MirrorCS"),sQuery(id+"F49.wireOp",EDGE,"E69"),sQuery(id+"F50.wireOp",EDGE,"E76.MirrorCS"),sQuery(id+"F50.wireOp",EDGE,"E80")])]});
            var Q2;
            Q2=makeQuery(id+"F51.opLoft","SWEPT_EDGE",EDGE,{"disambiguationData":[OSD([sQuery(id+"F47.wireOp",EDGE,"E64.3"),sQuery(id+"F49.wireOp",EDGE,"E66"),sQuery(id+"F49.wireOp",EDGE,"E68"),sQuery(id+"F50.wireOp",EDGE,"E73"),sQuery(id+"F50.wireOp",EDGE,"E79")])]});
            var Q3;
            Q3=makeQuery(id+"F51.opLoft","SWEPT_EDGE",EDGE,{"disambiguationData":[OSD([sQuery(id+"F49.wireOp",EDGE,"E70"),sQuery(id+"F49.wireOp",EDGE,"E71"),sQuery(id+"F50.wireOp",EDGE,"E81"),sQuery(id+"F50.wireOp",EDGE,"E82")])]});
            var Q4;
            Q4=makeQuery(id+"F51.opLoft","SWEPT_EDGE",EDGE,{"disambiguationData":[OSD([sQuery(id+"F47.wireOp",EDGE,"E64.0"),sQuery(id+"F49.wireOp",EDGE,"E67.MirrorCS"),sQuery(id+"F49.wireOp",EDGE,"E70"),sQuery(id+"F50.wireOp",EDGE,"E76.MirrorCS"),sQuery(id+"F50.wireOp",EDGE,"E81")])]});
            var Q5;
            Q5=makeQuery(id+"F51.opLoft","SWEPT_EDGE",EDGE,{"disambiguationData":[OSD([sQuery(id+"F47.wireOp",EDGE,"E64.1"),sQuery(id+"F49.wireOp",EDGE,"E66"),sQuery(id+"F49.wireOp",EDGE,"E71"),sQuery(id+"F50.wireOp",EDGE,"E73"),sQuery(id+"F50.wireOp",EDGE,"E82")])]});
            fillet(context, id + "F52", {"entities" : qUnion([Q0, Q1, Q2, Q3, Q4, Q5]), "radius" : 0.5 * mm, "tangentPropagation" : true, "allowEdgeOverflow" : false});
        }
        {
            var Q0;
            Q0=makeQuery(id+"F51.opLoft","MID_CAP_EDGE",EDGE,{"disambiguationData":[OSD([sQuery(id+"F47.wireOp",EDGE,"E64.1"),sQuery(id+"F47.wireOp",EDGE,"E64.3"),sQuery(id+"F49.wireOp",EDGE,"E66"),sQuery(id+"F49.wireOp",EDGE,"E68"),sQuery(id+"F49.wireOp",EDGE,"E71")])],"capPos":0.0});
            var Q1;
            Q1=makeQuery(id+"F51.opLoft","MID_CAP_EDGE",EDGE,{"disambiguationData":[OSD([sQuery(id+"F47.wireOp",EDGE,"E64.0"),sQuery(id+"F47.wireOp",EDGE,"E64.4"),sQuery(id+"F49.wireOp",EDGE,"E67.MirrorCS"),sQuery(id+"F49.wireOp",EDGE,"E69"),sQuery(id+"F49.wireOp",EDGE,"E70")])],"capPos":0.0});
            fillet(context, id + "F53", {"entities" : qUnion([Q0, Q1]), "radius" : 3 * mm, "tangentPropagation" : true, "allowEdgeOverflow" : false});
        }
        {
            var Q0;
            Q0=makeQuery(id+"F51.opLoft","MID_CAP_EDGE",EDGE,{"disambiguationData":[OSD([sQuery(id+"F50.wireOp",EDGE,"E73"),sQuery(id+"F50.wireOp",EDGE,"E79"),sQuery(id+"F50.wireOp",EDGE,"E82")])],"capPos":1.0});
            fillet(context, id + "F54", {"entities" : qUnion([Q0]), "radius" : 0.5 * mm, "tangentPropagation" : true, "allowEdgeOverflow" : false});
        }
    });
